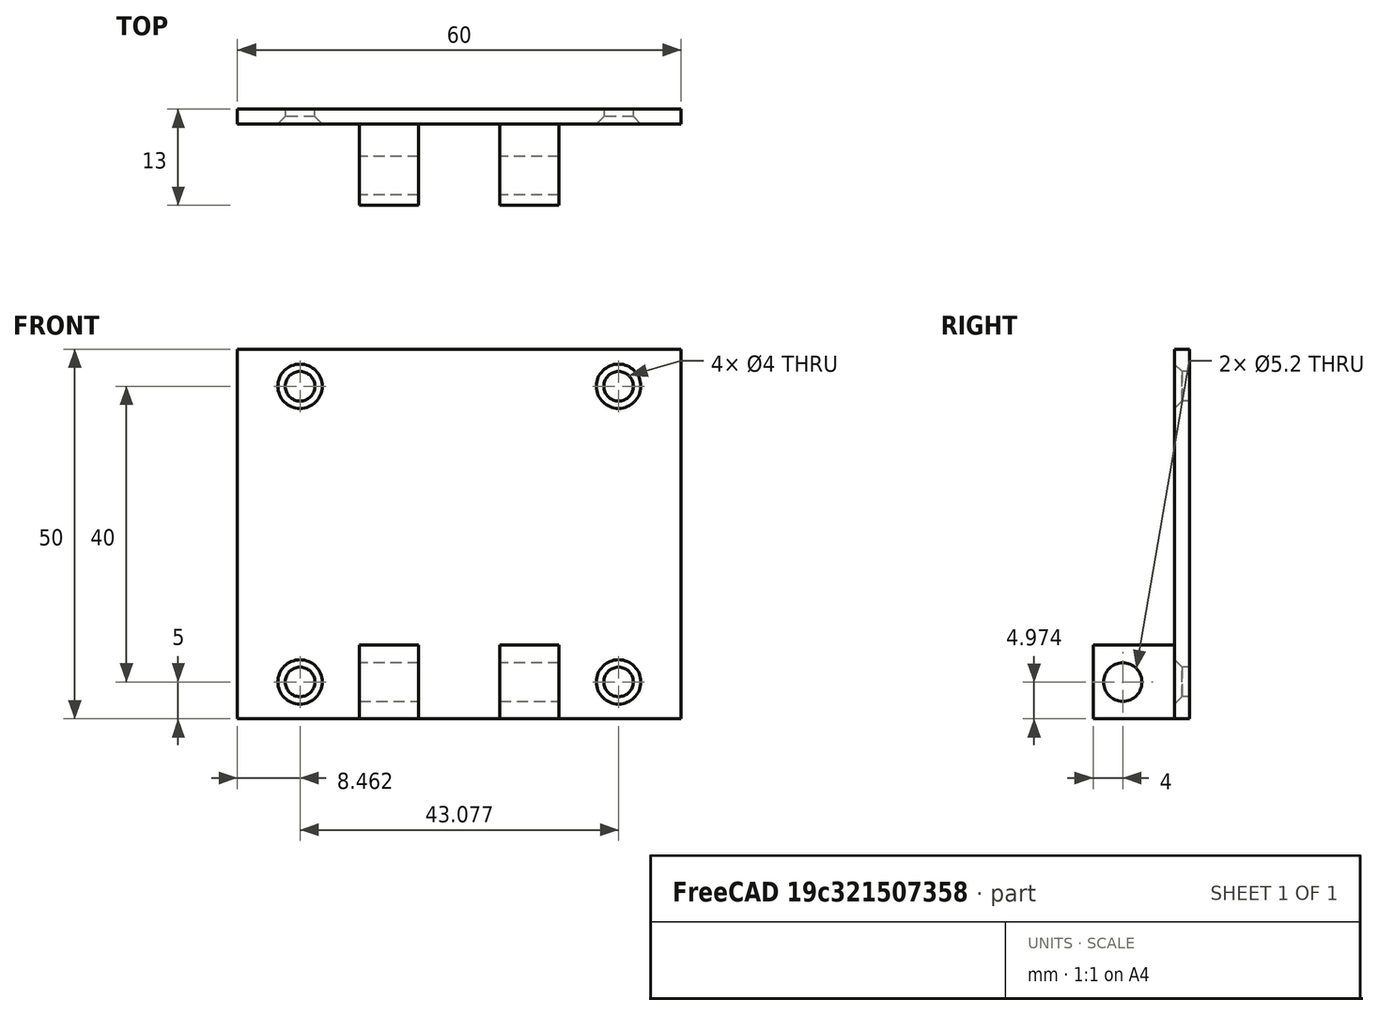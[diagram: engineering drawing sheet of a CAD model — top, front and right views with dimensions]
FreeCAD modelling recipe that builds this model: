
FCSTD DOCUMENT  (FreeCAD 0.20R29603 (Git))
Label: frameFixation
License: All rights reserved
LicenseURL: http://en.wikipedia.org/wiki/All_rights_reserved
objects: TechDraw::DrawViewDimension×14, Sketcher::SketchObject×4, TechDraw::DrawProjGroupItem×3, PartDesign::Pad×2, PartDesign::Pocket×2, PartDesign::Chamfer×1, PartDesign::Body×1, TechDraw::DrawSVGTemplate×1, TechDraw::DrawProjGroup×1, TechDraw::DrawPage×1
note: 15 computed .brp shape members not serialized (recipe doc carries the construction recipe); baked Part::Feature solids carry a one-line shape summary decoded from their .brp

FEATURE [Sketcher::SketchObject] Sketch
  FullyConstrained = true
  MapMode = 5
  Placement = pos=(0,0,0) rot=(1,0,0;1.5708rad)
  Support = -> [XZ_Plane]
  sketch-geometry (4):
    g0: LineSegment StartX=0 StartY=0 StartZ=0 EndX=60 EndY=0 EndZ=0
    g1: LineSegment StartX=0 StartY=50 StartZ=0 EndX=60 EndY=50 EndZ=0
    g2: LineSegment StartX=0 StartY=0 StartZ=0 EndX=0 EndY=50 EndZ=0
    g3: LineSegment StartX=60 StartY=50 StartZ=0 EndX=60 EndY=0 EndZ=0
  constraints (11):
    c: Coincident(g0,g-1)
    c: PointOnObject(g0,g-1)
    c: Distance(g0) = 60
    c: PointOnObject(g1,g-2)
    c: Horizontal(g1)
    c: Equal(g0,g1)
    c: DistanceY(g0,g1) = 50
    c: Coincident(g2,g0)
    c: Coincident(g2,g1)
    c: Coincident(g3,g1)
    c: Coincident(g3,g0)
FEATURE [PartDesign::Pad] Pad
  Direction = (1,1,1)
  Length = 2
  Length2 = 100
  Placement = pos=(0,0,0) rot=(1,0,0;1.5708rad)
  Profile = -> Sketch
  Type = 0
FEATURE [Sketcher::SketchObject] Sketch001
  FullyConstrained = true
  MapMode = 5
  Placement = pos=(0,-2,0) rot=(1,0,0;1.5708rad)
  Support = -> [Pad]
  sketch-geometry (8):
    g0: LineSegment StartX=16.5 StartY=0 StartZ=0 EndX=24.5 EndY=0 EndZ=0
    g1: LineSegment StartX=35.5 StartY=0 StartZ=0 EndX=43.5 EndY=0 EndZ=0
    g2: LineSegment StartX=16.5 StartY=0 StartZ=0 EndX=16.5 EndY=10 EndZ=0
    g3: LineSegment StartX=24.5 StartY=0 StartZ=0 EndX=24.5 EndY=10 EndZ=0
    g4: LineSegment StartX=35.5 StartY=0 StartZ=0 EndX=35.5 EndY=10 EndZ=0
    g5: LineSegment StartX=43.5 StartY=0 StartZ=0 EndX=43.5 EndY=10 EndZ=0
    g6: LineSegment StartX=16.5 StartY=10 StartZ=0 EndX=24.5 EndY=10 EndZ=0
    g7: LineSegment StartX=35.5 StartY=10 StartZ=0 EndX=43.5 EndY=10 EndZ=0
  constraints (24):
    c: PointOnObject(g0,g-1)
    c: PointOnObject(g0,g-1)
    c: Distance(g0) = 8
    c: DistanceX(g-1,g0) = 24.5
    c: PointOnObject(g1,g-1)
    c: PointOnObject(g1,g-1)
    c: Equal(g0,g1)
    c: DistanceX(g0,g1) = 11
    c: Coincident(g2,g0)
    c: Vertical(g2)
    c: Distance(g2) = 10
    c: Coincident(g3,g0)
    c: Vertical(g3)
    c: Coincident(g4,g1)
    c: Coincident(g5,g1)
    c: Vertical(g5)
    c: Equal(g2,g3)
    c: Equal(g3,g4)
    c: Equal(g4,g5)
    c: Vertical(g4)
    c: Coincident(g6,g2)
    c: Coincident(g6,g3)
    c: Coincident(g7,g4)
    c: Coincident(g7,g5)
FEATURE [PartDesign::Pad] Pad001
  BaseFeature = -> Pad
  Direction = (1,1,1)
  Length = 11
  Length2 = 100
  Placement = pos=(0,0,0) rot=(1,0,0;1.5708rad)
  Profile = -> Sketch001
  Type = 0
FEATURE [Sketcher::SketchObject] Sketch002
  FullyConstrained = false
  MapMode = 5
  Placement = pos=(16.5,0,0) rot=(0.707107,0,-0.707107;3.14159rad)
  Support = -> [Pad001]
  sketch-geometry (1):
    g0: Circle CenterX=-4.9743 CenterY=9 CenterZ=0 NormalX=0 NormalY=0 NormalZ=1 AngleXU=0 Radius=2.6
  constraints (2):
    c: Diameter(g0) = 5.2
    c: DistanceY(g-1,g0) = 9
FEATURE [PartDesign::Pocket] Pocket
  BaseFeature = -> Pad001
  Direction = (1,1,1)
  Length = 5
  Length2 = 100
  Placement = pos=(0,0,0) rot=(1,0,0;1.5708rad)
  Profile = -> Sketch002
  Type = 1
FEATURE [Sketcher::SketchObject] Sketch003
  ExternalGeometry = -> [Pocket]
  FullyConstrained = false
  MapMode = 5
  Placement = pos=(0,-2,0) rot=(1,0,0;1.5708rad)
  Support = -> [Pocket]
  sketch-geometry (15):
    g0: LineSegment StartX=0 StartY=4e-16 StartZ=0 EndX=60 EndY=0 EndZ=0
    g1: Circle CenterX=8.46167 CenterY=5 CenterZ=0 NormalX=0 NormalY=0 NormalZ=1 AngleXU=0 Radius=2
    g2: Circle CenterX=51.5383 CenterY=5 CenterZ=0 NormalX=0 NormalY=0 NormalZ=1 AngleXU=0 Radius=2
    g3: Circle CenterX=51.5383 CenterY=45 CenterZ=0 NormalX=0 NormalY=0 NormalZ=1 AngleXU=0 Radius=2
    g4: Circle CenterX=8.46167 CenterY=45 CenterZ=0 NormalX=0 NormalY=0 NormalZ=1 AngleXU=0 Radius=2
    g5: LineSegment StartX=8.46167 StartY=45 StartZ=0 EndX=8.46167 EndY=50 EndZ=0
    g6: LineSegment StartX=8.46167 StartY=45 StartZ=0 EndX=0 EndY=45 EndZ=0
    g7: LineSegment StartX=51.5383 StartY=45 StartZ=0 EndX=51.5383 EndY=50 EndZ=0
    g8: LineSegment StartX=51.5383 StartY=45 StartZ=0 EndX=60 EndY=45 EndZ=0
    g9: LineSegment StartX=51.5383 StartY=5 StartZ=0 EndX=51.5383 EndY=-4.25757e-11 EndZ=0
    g10: LineSegment StartX=51.5383 StartY=5 StartZ=0 EndX=60 EndY=5 EndZ=0
    g11: LineSegment StartX=8.46167 StartY=5 StartZ=0 EndX=8.46167 EndY=-2.16653e-11 EndZ=0
    g12: LineSegment StartX=8.46167 StartY=5 StartZ=0 EndX=0 EndY=5 EndZ=0
    g13: LineSegment StartX=16.5 StartY=10 StartZ=0 EndX=0 EndY=10 EndZ=0
    g14: LineSegment StartX=8.46167 StartY=5 StartZ=0 EndX=8.46167 EndY=10 EndZ=0
  constraints (43):
    c: Coincident(g0,g-5)
    c: Coincident(g0,g-4)
    c: Diameter(g4) = 4
    c: Diameter(g3) = 4
    c: Diameter(g2) = 4
    c: Diameter(g1) = 4
    c: Coincident(g5,g4)
    c: PointOnObject(g5,g-3)
    c: Vertical(g5)
    c: Coincident(g6,g4)
    c: PointOnObject(g6,g-5)
    c: Horizontal(g6)
    c: Coincident(g7,g3)
    c: PointOnObject(g7,g-3)
    c: Vertical(g7)
    c: Coincident(g8,g3)
    c: PointOnObject(g8,g-4)
    c: Horizontal(g8)
    c: Coincident(g9,g2)
    c: PointOnObject(g9,g0)
    c: Vertical(g9)
    c: Coincident(g10,g2)
    c: PointOnObject(g10,g-4)
    c: Horizontal(g10)
    c: Coincident(g11,g1)
    c: PointOnObject(g11,g0)
    c: Vertical(g11)
    c: Coincident(g12,g1)
    c: PointOnObject(g12,g-5)
    c: Horizontal(g12)
    c: Equal(g6,g8)
    c: Equal(g12,g10)
    c: Equal(g12,g6)
    c: Equal(g5,g7)
    c: Equal(g9,g11)
    c: Equal(g11,g5)
    c: Coincident(g13,g-6)
    c: PointOnObject(g13,g-5)
    c: Horizontal(g13)
    c: Coincident(g14,g1)
    c: PointOnObject(g14,g13)
    c: Vertical(g14)
    c: Equal(g14,g11)
FEATURE [PartDesign::Pocket] Pocket001
  BaseFeature = -> Pocket
  Direction = (0,1,-2e-16)
  Length = 5
  Length2 = 5
  Placement = pos=(0,0,0) rot=(1,0,0;1.5708rad)
  Profile = -> Sketch003
  ReferenceAxis = -> Sketch003 [N_Axis]
  Type = 1
FEATURE [PartDesign::Chamfer] Chamfer
  Angle = 45
  Base = -> Pocket001 [Edge27,Edge29,Edge30,Edge28]
  BaseFeature = -> Pocket001
  ChamferType = 0
  FlipDirection = false
  Placement = pos=(0,0,0) rot=(1,0,0;1.5708rad)
  Size = 1
  Size2 = 1
  SupportTransform = false
  UseAllEdges = false
FEATURE [PartDesign::Body] Body
  Group = -> [Sketch,Pad,Sketch001,Pad001,Sketch002,Pocket,Sketch003,Pocket001,Chamfer]
  Origin = -> Origin
  Tip = -> Chamfer
FEATURE [TechDraw::DrawSVGTemplate] Template
  EditableTexts = Designed_by_Name=Белкин Никита; FC-Date=16.04.2023; FC-SC=1:1; FC-Title=Крепление к раме
  Height = 210
  Orientation = 1
  Width = 297
FEATURE [TechDraw::DrawProjGroupItem] ProjItem  label="Front"
  CoarseView = false
  Direction = (0,-1,0)
  Focus = 100
  HardHidden = false
  IsoCount = 0
  IsoHidden = false
  IsoVisible = false
  LockPosition = true
  Perspective = false
  Rotation = 0
  RotationVector = (1,0,0)
  ScaleType = 2
  SeamHidden = false
  SeamVisible = true
  SmoothHidden = false
  SmoothVisible = true
  Source = -> [Body]
  Type = 0
  X = 0
  XDirection = (1,0,0)
  Y = 0
FEATURE [TechDraw::DrawProjGroupItem] ProjItem001  label="Top"
  CoarseView = false
  Direction = (0,0,1)
  Focus = 100
  HardHidden = false
  IsoCount = 0
  IsoHidden = false
  IsoVisible = false
  LockPosition = false
  Perspective = false
  Rotation = 0
  RotationVector = (1,0,0)
  ScaleType = 2
  SeamHidden = false
  SeamVisible = true
  SmoothHidden = false
  SmoothVisible = true
  Source = -> [Body]
  Type = 4
  X = 0
  XDirection = (1,0,0)
  Y = -65
FEATURE [TechDraw::DrawProjGroupItem] ProjItem002  label="Left"
  CoarseView = false
  Direction = (-1,-1e-16,0)
  Focus = 100
  HardHidden = false
  IsoCount = 0
  IsoHidden = false
  IsoVisible = false
  LockPosition = false
  Perspective = false
  Rotation = 0
  RotationVector = (1,0,0)
  ScaleType = 2
  SeamHidden = false
  SeamVisible = true
  SmoothHidden = false
  SmoothVisible = true
  Source = -> [Body]
  Type = 1
  X = 59.8921
  XDirection = (1e-16,-1,0)
  Y = 0
FEATURE [TechDraw::DrawProjGroup] ProjGroup
  Anchor = -> ProjItem
  AutoDistribute = true
  LockPosition = false
  ProjectionType = 0
  Rotation = 0
  ScaleType = 0
  Source = -> [Body]
  Views = -> [ProjItem,ProjItem001,ProjItem002]
  X = 94.64
  Y = 146.944
  spacingX = 15
  spacingY = 15
FEATURE [TechDraw::DrawViewDimension] Dimension
  AngleOverride = false
  Arbitrary = false
  ArbitraryTolerances = false
  EqualTolerance = true
  ExtensionAngle = 0
  FormatSpec = %.2w
  FormatSpecOverTolerance = %+.2w
  FormatSpecUnderTolerance = %+.2w
  Inverted = false
  LineAngle = 0
  LockPosition = false
  MeasureType = 1
  OverTolerance = 0
  References2D = -> [ProjItem]
  Rotation = 0
  ScaleType = 0
  TheoreticalExact = false
  Type = 1
  UnderTolerance = 0
  X = -0.629496
  Y = 39.6703
FEATURE [TechDraw::DrawViewDimension] Dimension001
  AngleOverride = false
  Arbitrary = false
  ArbitraryTolerances = false
  EqualTolerance = true
  ExtensionAngle = 0
  FormatSpec = %.2w
  FormatSpecOverTolerance = %+.2w
  FormatSpecUnderTolerance = %+.2w
  Inverted = false
  LineAngle = 0
  LockPosition = false
  MeasureType = 1
  OverTolerance = 0
  References2D = -> [ProjItem]
  Rotation = 0
  ScaleType = 0
  TheoreticalExact = false
  Type = 2
  UnderTolerance = 0
  X = -41.7506
  Y = 2.08034
FEATURE [TechDraw::DrawViewDimension] Dimension002
  AngleOverride = false
  Arbitrary = false
  ArbitraryTolerances = false
  EqualTolerance = true
  ExtensionAngle = 0
  FormatSpec = ⌀%.2w
  FormatSpecOverTolerance = %+.2w
  FormatSpecUnderTolerance = %+.2w
  Inverted = false
  LineAngle = 0
  LockPosition = false
  MeasureType = 1
  OverTolerance = 0
  References2D = -> [ProjItem]
  Rotation = 0
  ScaleType = 0
  TheoreticalExact = false
  Type = 5
  UnderTolerance = 0
  X = 6.71463
  Y = 0.839329
FEATURE [TechDraw::DrawViewDimension] Dimension003
  AngleOverride = false
  Arbitrary = false
  ArbitraryTolerances = false
  EqualTolerance = true
  ExtensionAngle = 0
  FormatSpec = ⌀%.2w
  FormatSpecOverTolerance = %+.2w
  FormatSpecUnderTolerance = %+.2w
  Inverted = false
  LineAngle = 0
  LockPosition = false
  MeasureType = 1
  OverTolerance = 0
  References2D = -> [ProjItem]
  Rotation = 0
  ScaleType = 0
  TheoreticalExact = false
  Type = 5
  UnderTolerance = 0
  X = 20.5635
  Y = 6.5048
FEATURE [TechDraw::DrawViewDimension] Dimension004
  AngleOverride = false
  Arbitrary = false
  ArbitraryTolerances = false
  EqualTolerance = true
  ExtensionAngle = 0
  FormatSpec = %.2w
  FormatSpecOverTolerance = %+.2w
  FormatSpecUnderTolerance = %+.2w
  Inverted = false
  LineAngle = 0
  LockPosition = false
  MeasureType = 1
  OverTolerance = 0
  References2D = -> [ProjItem002]
  Rotation = 0
  ScaleType = 0
  TheoreticalExact = false
  Type = 2
  UnderTolerance = 0
  X = 12.5575
  Y = -30.6495
FEATURE [TechDraw::DrawViewDimension] Dimension005
  AngleOverride = false
  Arbitrary = false
  ArbitraryTolerances = false
  EqualTolerance = true
  ExtensionAngle = 0
  FormatSpec = %.2w
  FormatSpecOverTolerance = %+.2w
  FormatSpecUnderTolerance = %+.2w
  Inverted = false
  LineAngle = 0
  LockPosition = false
  MeasureType = 1
  OverTolerance = 0
  References2D = -> [ProjItem002]
  Rotation = 0
  ScaleType = 0
  TheoreticalExact = false
  Type = 1
  UnderTolerance = 0
  X = 2.02628
  Y = 35.8933
FEATURE [TechDraw::DrawViewDimension] Dimension006
  AngleOverride = false
  Arbitrary = false
  ArbitraryTolerances = false
  EqualTolerance = true
  ExtensionAngle = 0
  FormatSpec = %.2w
  FormatSpecOverTolerance = %+.2w
  FormatSpecUnderTolerance = %+.2w
  Inverted = false
  LineAngle = 0
  LockPosition = false
  MeasureType = 1
  OverTolerance = 0
  References2D = -> [ProjItem002]
  Rotation = 0
  ScaleType = 0
  TheoreticalExact = false
  Type = 2
  UnderTolerance = 0
  X = 5.82404
  Y = 7.32514
FEATURE [TechDraw::DrawViewDimension] Dimension007
  AngleOverride = false
  Arbitrary = false
  ArbitraryTolerances = false
  EqualTolerance = true
  ExtensionAngle = 0
  FormatSpec = %.2w
  FormatSpecOverTolerance = %+.2w
  FormatSpecUnderTolerance = %+.2w
  Inverted = false
  LineAngle = 0
  LockPosition = false
  MeasureType = 1
  OverTolerance = 0
  References2D = -> [ProjItem002]
  Rotation = 0
  ScaleType = 0
  TheoreticalExact = false
  Type = 1
  UnderTolerance = 0
  X = -7.56085
  Y = -35.0899
FEATURE [TechDraw::DrawViewDimension] Dimension008
  AngleOverride = false
  Arbitrary = false
  ArbitraryTolerances = false
  EqualTolerance = true
  ExtensionAngle = 0
  FormatSpec = %.2w
  FormatSpecOverTolerance = %+.2w
  FormatSpecUnderTolerance = %+.2w
  Inverted = false
  LineAngle = 0
  LockPosition = false
  MeasureType = 1
  OverTolerance = 0
  References2D = -> [ProjItem001]
  Rotation = 0
  ScaleType = 0
  TheoreticalExact = false
  Type = 1
  UnderTolerance = 0
  X = -19.1872
  Y = -14.429
FEATURE [TechDraw::DrawViewDimension] Dimension009
  AngleOverride = false
  Arbitrary = false
  ArbitraryTolerances = false
  EqualTolerance = true
  ExtensionAngle = 0
  FormatSpec = %.2w
  FormatSpecOverTolerance = %+.2w
  FormatSpecUnderTolerance = %+.2w
  Inverted = false
  LineAngle = 0
  LockPosition = false
  MeasureType = 1
  OverTolerance = 0
  References2D = -> [ProjItem001]
  Rotation = 0
  ScaleType = 0
  TheoreticalExact = false
  Type = 1
  UnderTolerance = 0
  X = 18.5927
  Y = -11.3514
FEATURE [TechDraw::DrawViewDimension] Dimension010
  AngleOverride = false
  Arbitrary = false
  ArbitraryTolerances = false
  EqualTolerance = true
  ExtensionAngle = 0
  FormatSpec = %.2w
  FormatSpecOverTolerance = %+.2w
  FormatSpecUnderTolerance = %+.2w
  Inverted = false
  LineAngle = 0
  LockPosition = false
  MeasureType = 1
  OverTolerance = 0
  References2D = -> [ProjItem]
  Rotation = 0
  ScaleType = 0
  TheoreticalExact = false
  Type = 1
  UnderTolerance = 0
  X = -22.3795
  Y = -36.3489
FEATURE [TechDraw::DrawViewDimension] Dimension011
  AngleOverride = false
  Arbitrary = false
  ArbitraryTolerances = false
  EqualTolerance = true
  ExtensionAngle = 0
  FormatSpec = %.2w
  FormatSpecOverTolerance = %+.2w
  FormatSpecUnderTolerance = %+.2w
  Inverted = false
  LineAngle = 0
  LockPosition = false
  MeasureType = 1
  OverTolerance = 0
  References2D = -> [ProjItem]
  Rotation = 0
  ScaleType = 0
  TheoreticalExact = false
  Type = 1
  UnderTolerance = 0
  X = 21.1205
  Y = -36.3489
FEATURE [TechDraw::DrawViewDimension] Dimension012
  AngleOverride = false
  Arbitrary = false
  ArbitraryTolerances = false
  EqualTolerance = true
  ExtensionAngle = 0
  FormatSpec = %.2w
  FormatSpecOverTolerance = %+.2w
  FormatSpecUnderTolerance = %+.2w
  Inverted = false
  LineAngle = 0
  LockPosition = false
  MeasureType = 1
  OverTolerance = 0
  References2D = -> [ProjItem]
  Rotation = 0
  ScaleType = 0
  TheoreticalExact = false
  Type = 1
  UnderTolerance = 0
  X = -0.419664
  Y = -36.5588
FEATURE [TechDraw::DrawViewDimension] Dimension013
  AngleOverride = false
  Arbitrary = false
  ArbitraryTolerances = false
  EqualTolerance = true
  ExtensionAngle = 0
  FormatSpec = ⌀%.2w
  FormatSpecOverTolerance = %+.2w
  FormatSpecUnderTolerance = %+.2w
  Inverted = false
  LineAngle = 0
  LockPosition = false
  MeasureType = 1
  OverTolerance = 0
  References2D = -> [ProjItem002]
  Rotation = 0
  ScaleType = 0
  TheoreticalExact = false
  Type = 5
  UnderTolerance = 0
  X = -13.4293
  Y = -4.61631
FEATURE [TechDraw::DrawPage] Page
  KeepUpdated = true
  NextBalloonIndex = 1
  ProjectionType = 0
  Template = -> Template
  Views = -> [ProjGroup,Dimension,Dimension001,Dimension002,Dimension003,Dimension004,Dimension005,Dimension006,Dimension007,Dimension008,Dimension009,Dimension010,Dimension011,Dimension012,Dimension013]
